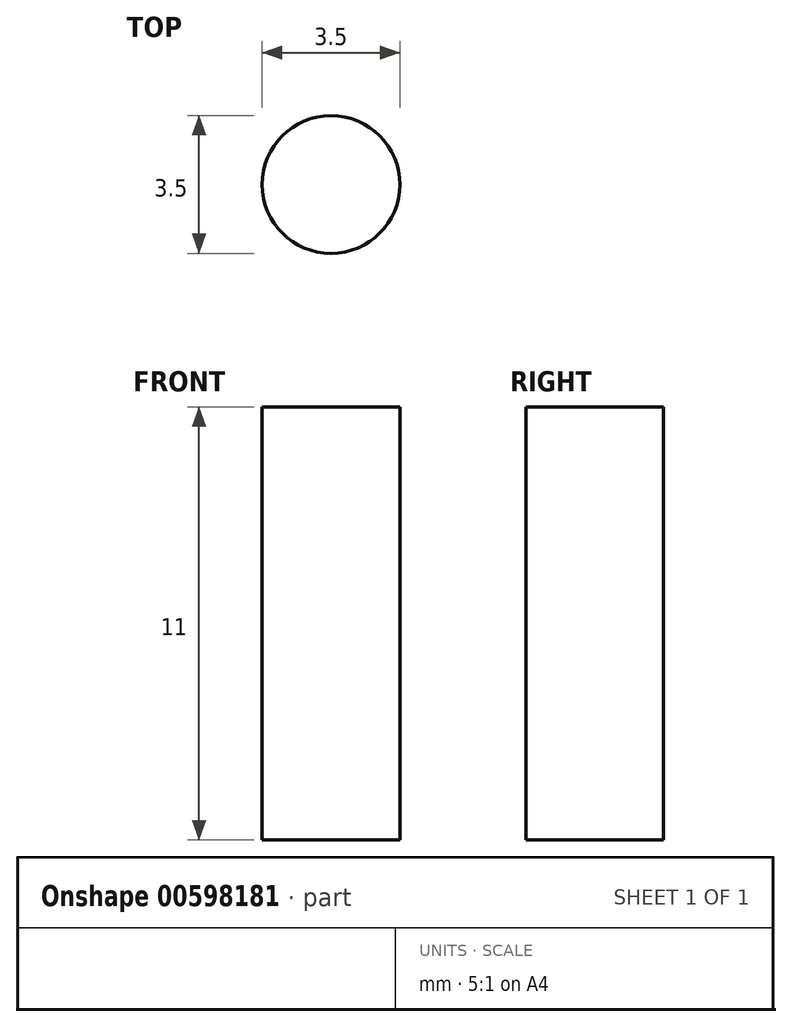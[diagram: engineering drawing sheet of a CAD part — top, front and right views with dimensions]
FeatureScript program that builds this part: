
annotation { "Feature Type Name" : "Feature", "Feature Type Description" : "" }
export const myFeature = defineFeature(function(context is Context, id is Id, definition is map)
    precondition{}
    {
        {
            var Q0;
            Q0=qCreatedBy(makeId("Top.planeOp"),FACE);
            var sketch = newSketch(context, id + "F0", { "sketchPlane" : qUnion([Q0])});
            skCircle(sketch, "E0", {"center": v(0, 0) * mm, "radius": 1.75 * mm});
            skSolve(sketch);
        }
        {
            var Q0;
            Q0 = qSketchRegion(id + "F0", true);
            extrude(context, id + "F1", {"entities" : qUnion([Q0]), "depth" : 11 * mm, "offsetDistance" : 25 * mm});
        }
    });
